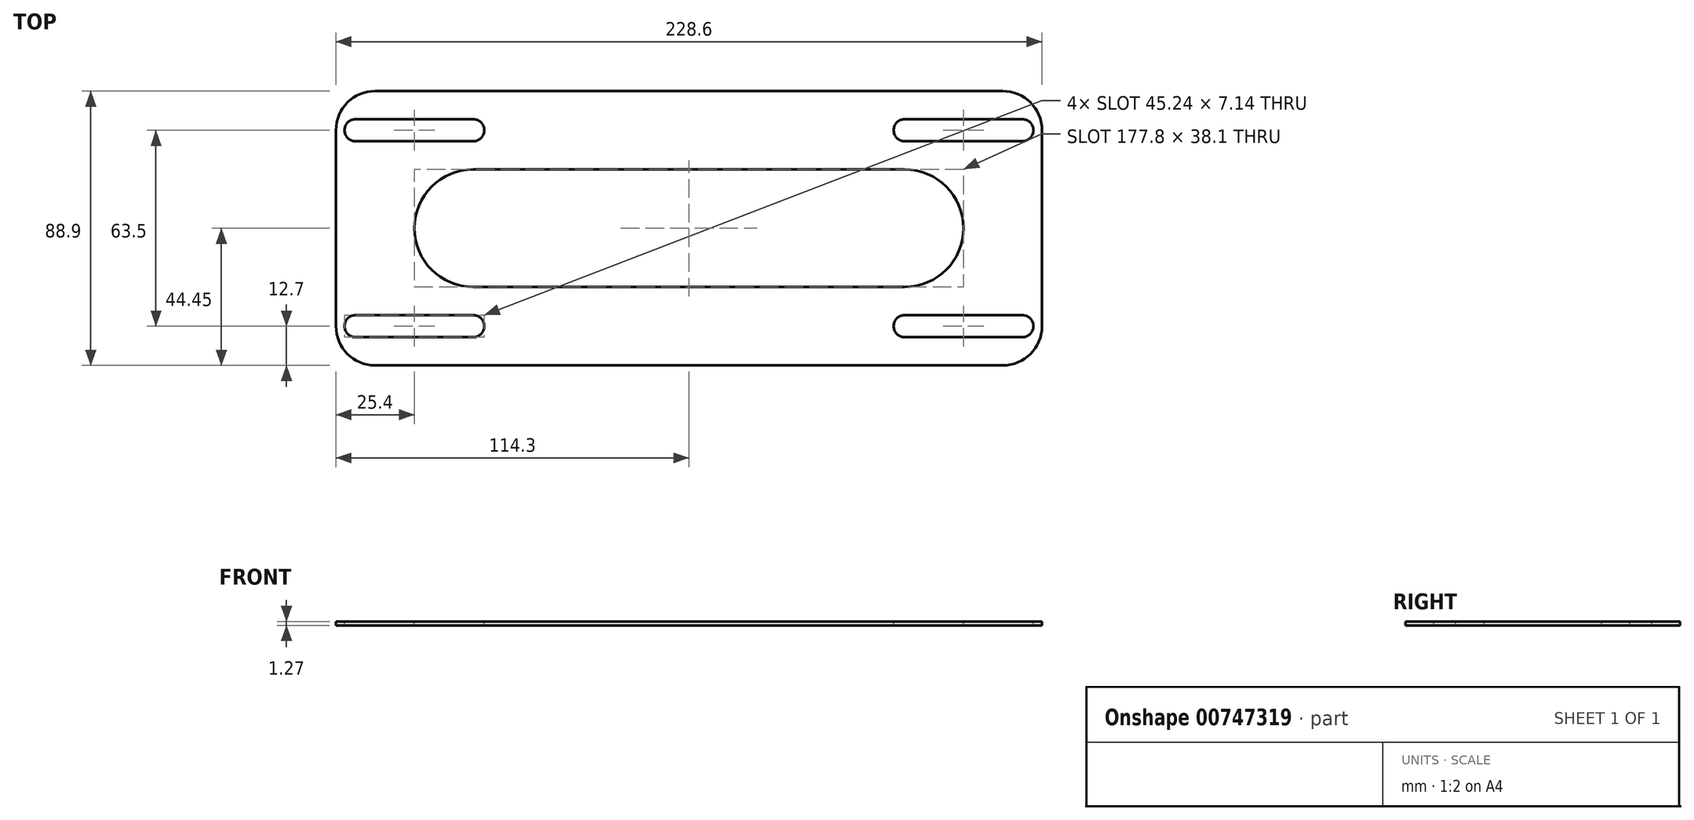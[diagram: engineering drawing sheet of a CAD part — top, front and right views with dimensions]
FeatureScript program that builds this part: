
annotation { "Feature Type Name" : "Feature", "Feature Type Description" : "" }
export const myFeature = defineFeature(function(context is Context, id is Id, definition is map)
    precondition{}
    {
        {
            var Q0;
            Q0=qCreatedBy(makeId("Top.planeOp"),FACE);
            var sketch = newSketch(context, id + "F0", { "sketchPlane" : qUnion([Q0])});
            skLineSegment(sketch, "E0.bottom", {"start": v(0, 0) * mm, "end": v(228.6, 0) * mm});
            skLineSegment(sketch, "E0.top", {"start": v(0, 88.9) * mm, "end": v(228.6, 88.9) * mm});
            skLineSegment(sketch, "E0.left", {"start": v(0, 0) * mm, "end": v(0, 88.9) * mm});
            skLineSegment(sketch, "E0.right", {"start": v(228.6, 0) * mm, "end": v(228.6, 88.9) * mm});
            skSolve(sketch);
        }
        {
            var Q0;
            Q0=qSketchRegion(id+"F0",true);
            extrude(context, id + "F1", {"entities" : qUnion([Q0]), "depth" : 1.27 * mm, "offsetDistance" : 25.4 * mm});
        }
        {
            var Q0;
            Q0=makeQuery(id+"F1.opExtrude","SWEPT_EDGE",EDGE,{"disambiguationData":[OSD([sQuery(id+"F0.wireOp",EDGE,"E0.bottom"),sQuery(id+"F0.wireOp",EDGE,"E0.right")])]});
            var Q1;
            Q1=makeQuery(id+"F1.opExtrude","SWEPT_EDGE",EDGE,{"disambiguationData":[OSD([sQuery(id+"F0.wireOp",EDGE,"E0.top"),sQuery(id+"F0.wireOp",EDGE,"E0.right")])]});
            var Q2;
            Q2=makeQuery(id+"F1.opExtrude","SWEPT_EDGE",EDGE,{"disambiguationData":[OSD([sQuery(id+"F0.wireOp",EDGE,"E0.top"),sQuery(id+"F0.wireOp",EDGE,"E0.left")])]});
            var Q3;
            Q3=makeQuery(id+"F1.opExtrude","SWEPT_EDGE",EDGE,{"disambiguationData":[OSD([sQuery(id+"F0.wireOp",EDGE,"E0.bottom"),sQuery(id+"F0.wireOp",EDGE,"E0.left")])]});
            fillet(context, id + "F2", {"entities" : qUnion([Q0, Q1, Q2, Q3]), "radius" : 12.7 * mm, "tangentPropagation" : true, "allowEdgeOverflow" : false});
        }
        {
            var Q0;
            Q0=makeQuery(id+"F1.opExtrude","CAP_FACE",FACE,{"disambiguationData":[OSD([sQuery(id+"F0.wireOp",EDGE,"E0.bottom"),sQuery(id+"F0.wireOp",EDGE,"E0.top"),sQuery(id+"F0.wireOp",EDGE,"E0.left"),sQuery(id+"F0.wireOp",EDGE,"E0.right")])],"isStart":false});
            var sketch = newSketch(context, id + "F3", { "sketchPlane" : qUnion([Q0])});
            skLineSegment(sketch, "E1", {"start": v(0, 44.45) * mm, "end": v(228.6, 44.45) * mm, "construction": true});
            skLineSegment(sketch, "E2", {"start": v(114.3, 88.9) * mm, "end": v(114.3, 0) * mm, "construction": true});
            skLineSegment(sketch, "E3", {"start": v(6.35, 16.27) * mm, "end": v(44.45, 16.27) * mm});
            skLineSegment(sketch, "E4", {"start": v(6.35, 9.13) * mm, "end": v(44.45, 9.13) * mm});
            skArc(sketch, "E5", {"start": v(6.35, 16.27) * mm, "mid": v(2.78, 12.7) * mm, "end": v(6.35, 9.13) * mm});
            skArc(sketch, "E6", {"start": v(44.45, 16.27) * mm, "mid": v(48.02, 12.7) * mm, "end": v(44.45, 9.13) * mm});
            skLineSegment(sketch, "E7.MirrorCS", {"start": v(6.35, 72.63) * mm, "end": v(44.45, 72.63) * mm});
            skLineSegment(sketch, "E8.MirrorCS", {"start": v(6.35, 79.77) * mm, "end": v(44.45, 79.77) * mm});
            skArc(sketch, "E9.MirrorCS", {"start": v(6.35, 72.63) * mm, "mid": v(2.78, 76.2) * mm, "end": v(6.35, 79.77) * mm});
            skArc(sketch, "E10.MirrorCS", {"start": v(44.45, 72.63) * mm, "mid": v(48.02, 76.2) * mm, "end": v(44.45, 79.77) * mm});
            skLineSegment(sketch, "E11.MirrorCS", {"start": v(222.25, 79.77) * mm, "end": v(184.15, 79.77) * mm});
            skLineSegment(sketch, "E12.MirrorCS", {"start": v(222.25, 72.63) * mm, "end": v(184.15, 72.63) * mm});
            skArc(sketch, "E13.MirrorCS", {"start": v(184.15, 72.63) * mm, "mid": v(180.58, 76.2) * mm, "end": v(184.15, 79.77) * mm});
            skArc(sketch, "E14.MirrorCS", {"start": v(222.25, 72.63) * mm, "mid": v(225.82, 76.2) * mm, "end": v(222.25, 79.77) * mm});
            skLineSegment(sketch, "E15.MirrorCS", {"start": v(222.25, 16.27) * mm, "end": v(184.15, 16.27) * mm});
            skArc(sketch, "E16.MirrorCS", {"start": v(222.25, 16.27) * mm, "mid": v(225.82, 12.7) * mm, "end": v(222.25, 9.13) * mm});
            skLineSegment(sketch, "E17.MirrorCS", {"start": v(222.25, 9.13) * mm, "end": v(184.15, 9.13) * mm});
            skArc(sketch, "E18.MirrorCS", {"start": v(184.15, 16.27) * mm, "mid": v(180.58, 12.7) * mm, "end": v(184.15, 9.13) * mm});
            skSolve(sketch);
        }
        {
            var Q0;
            Q0=qSketchRegion(id+"F3",true);
            extrude(context, id + "F4", {"entities" : qUnion([Q0]), "operationType" : NewBodyOperationType.REMOVE, "oppositeDirection" : true, "depth" : 25.4 * mm, "offsetDistance" : 25.4 * mm});
        }
        {
            var Q0;
            Q0=makeQuery(id+"F1.opExtrude","CAP_FACE",FACE,{"disambiguationData":[OSD([sQuery(id+"F0.wireOp",EDGE,"E0.bottom"),sQuery(id+"F0.wireOp",EDGE,"E0.top"),sQuery(id+"F0.wireOp",EDGE,"E0.left"),sQuery(id+"F0.wireOp",EDGE,"E0.right")])],"isStart":false});
            var sketch = newSketch(context, id + "F5", { "sketchPlane" : qUnion([Q0])});
            skLineSegment(sketch, "E19", {"start": v(0, 44.45) * mm, "end": v(228.6, 44.45) * mm, "construction": true});
            skLineSegment(sketch, "E20", {"start": v(114.3, 88.9) * mm, "end": v(114.3, 0) * mm, "construction": true});
            skLineSegment(sketch, "E21", {"start": v(44.45, 25.4) * mm, "end": v(114.3, 25.4) * mm});
            skLineSegment(sketch, "E22.MirrorCS", {"start": v(44.45, 63.5) * mm, "end": v(114.3, 63.5) * mm});
            skArc(sketch, "E23", {"start": v(44.45, 63.5) * mm, "mid": v(25.4, 44.45) * mm, "end": v(44.45, 25.4) * mm});
            skLineSegment(sketch, "E24.MirrorCS", {"start": v(184.15, 63.5) * mm, "end": v(114.3, 63.5) * mm});
            skArc(sketch, "E25.MirrorCS", {"start": v(184.15, 63.5) * mm, "mid": v(203.2, 44.45) * mm, "end": v(184.15, 25.4) * mm});
            skLineSegment(sketch, "E26.MirrorCS", {"start": v(184.15, 25.4) * mm, "end": v(114.3, 25.4) * mm});
            skSolve(sketch);
        }
        {
            var Q0;
            Q0=qSketchRegion(id+"F5",true);
            extrude(context, id + "F6", {"entities" : qUnion([Q0]), "operationType" : NewBodyOperationType.REMOVE, "endBound" : BoundingType.THROUGH_ALL, "oppositeDirection" : true, "depth" : 25.4 * mm, "offsetDistance" : 25.4 * mm});
        }
    });
